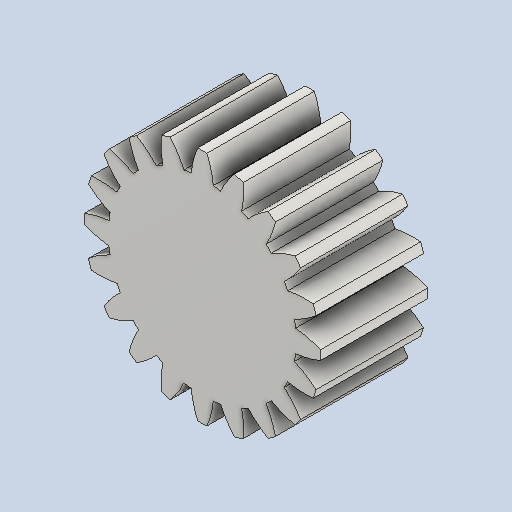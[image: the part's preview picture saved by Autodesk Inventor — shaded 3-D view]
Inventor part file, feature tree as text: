
AUTODESK INVENTOR PART (.ipt)
format: ipt  version: 2023 (Build 270158030, 158C)  size: 249,856 bytes
history: native  units: mm (DEFAULTED — no unit token found)
features: plane x3, other x3, sketch x2, extrude x1
ambient origin geometry x8: Origin, YZ Plane, XZ Plane, XY Plane, X Axis, Y Axis, Z Axis, Center Point
bodies: Solid1 (feature_tree)
feature tree (9):
  extrude  "Extrusion1"  Depth=20.0mm TaperAngle=0.0deg
  plane  "Work Plane2"
  plane  "Work Plane8"
  plane  "Work Plane9"
  other  "Spur Gear"
  sketch  "Sketch1"  dims[d0=44.0mm d1=20.0mm d2=0.0mm]
  sketch  "Sketch2"  dims[d3=40.0mm d4=10.0mm d5=0.0mm d16=100.0mm d17=0.0mm d34=1.570796mm d39=0.0mm d41=0.0mm d43=100.0mm d46=100.0mm d47=0.0mm d48=0.0mm]
  other  "Srf1"
  other  "Pitch Diameter"
